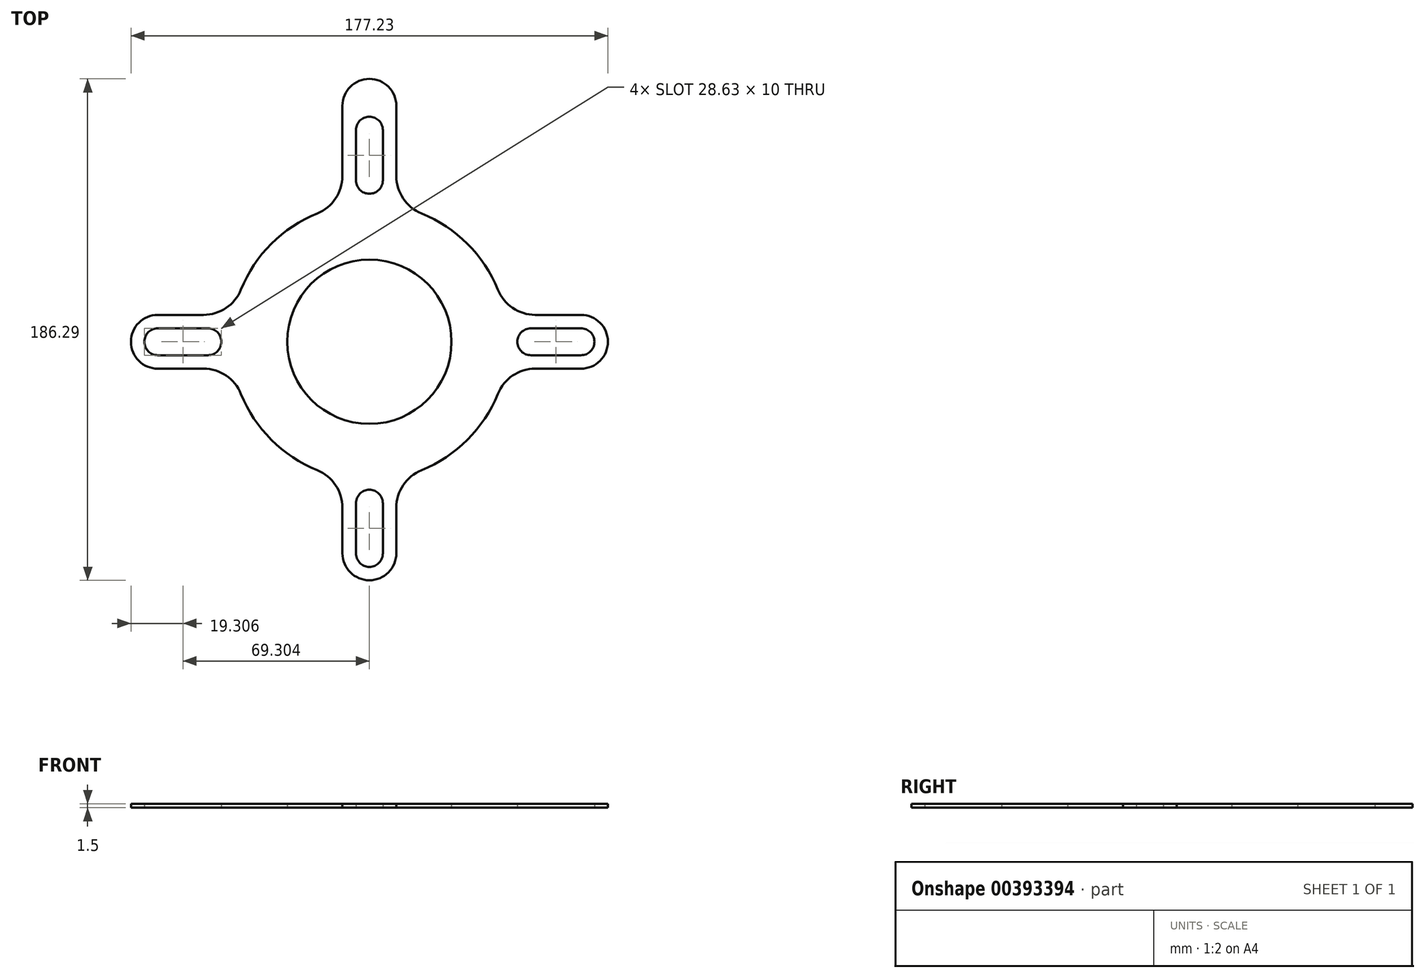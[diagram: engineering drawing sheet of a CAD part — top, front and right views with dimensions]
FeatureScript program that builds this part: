
annotation { "Feature Type Name" : "Feature", "Feature Type Description" : "" }
export const myFeature = defineFeature(function(context is Context, id is Id, definition is map)
    precondition{}
    {
        {
            var Q0;
            Q0=qCreatedBy(makeId("Top.planeOp"),FACE);
            var sketch = newSketch(context, id + "F0", { "sketchPlane" : qUnion([Q0])});
            skCircle(sketch, "E0", {"center": v(0, 0) * mm, "radius": 30.5 * mm});
            skArc(sketch, "E1", {"start": v(-19.36, 47.72) * mm, "mid": v(-36.42, 36.42) * mm, "end": v(-47.72, 19.36) * mm});
            skLineSegment(sketch, "E2", {"start": v(0, 0) * mm, "end": v(0, 75.54) * mm, "construction": true});
            skLineSegment(sketch, "E3", {"start": v(0, 0) * mm, "end": v(88.56, 0) * mm, "construction": true});
            skLineSegment(sketch, "E4", {"start": v(-10, 61.62) * mm, "end": v(-10, 76.12) * mm});
            skLineSegment(sketch, "E5", {"start": v(0, 97.68) * mm, "end": v(0, 97.68) * mm});
            skLineSegment(sketch, "E6", {"start": v(10, 76.12) * mm, "end": v(10, 61.62) * mm});
            skPoint(sketch, "E7.visualSharp", {"position": v(-10, 50.52) * mm});
            skArc(sketch, "E7.filletArc", {"start": v(-19.36, 47.72) * mm, "mid": v(-12.56, 53.24) * mm, "end": v(-10, 61.62) * mm});
            skPoint(sketch, "E8.visualSharp", {"position": v(10, 50.52) * mm});
            skArc(sketch, "E8.filletArc", {"start": v(10, 61.62) * mm, "mid": v(12.56, 53.24) * mm, "end": v(19.36, 47.72) * mm});
            skLineSegment(sketch, "E9.MirrorCS", {"start": v(10, -78.61) * mm, "end": v(10, -61.62) * mm});
            skLineSegment(sketch, "E10.MirrorCS", {"start": v(-10, -61.62) * mm, "end": v(-10, -78.61) * mm});
            skArc(sketch, "E11.MirrorCS", {"start": v(-19.36, -47.72) * mm, "mid": v(-12.56, -53.24) * mm, "end": v(-10, -61.62) * mm});
            skArc(sketch, "E12.MirrorCS", {"start": v(10, -61.62) * mm, "mid": v(12.56, -53.24) * mm, "end": v(19.36, -47.72) * mm});
            skArc(sketch, "E13.trimOffspring", {"start": v(19.36, -47.72) * mm, "mid": v(36.42, -36.42) * mm, "end": v(47.72, -19.36) * mm});
            skLineSegment(sketch, "E14", {"start": v(0, 0) * mm, "end": v(81.73, 81.73) * mm, "construction": true});
            skLineSegment(sketch, "E15.MirrorCS", {"start": v(78.62, 10) * mm, "end": v(61.62, 10) * mm});
            skArc(sketch, "E16.MirrorCS", {"start": v(61.62, 10) * mm, "mid": v(53.24, 12.56) * mm, "end": v(47.72, 19.36) * mm});
            skLineSegment(sketch, "E17.MirrorCS", {"start": v(61.62, -10) * mm, "end": v(78.62, -10) * mm});
            skArc(sketch, "E18.MirrorCS", {"start": v(47.72, -19.36) * mm, "mid": v(53.24, -12.56) * mm, "end": v(61.62, -10) * mm});
            skArc(sketch, "E19.trimOffspring", {"start": v(47.72, 19.36) * mm, "mid": v(36.42, 36.42) * mm, "end": v(19.36, 47.72) * mm});
            skLineSegment(sketch, "E20.MirrorCS", {"start": v(-78.61, 10) * mm, "end": v(-61.62, 10) * mm});
            skLineSegment(sketch, "E21.MirrorCS", {"start": v(-61.62, -10) * mm, "end": v(-78.61, -10) * mm});
            skArc(sketch, "E22.MirrorCS", {"start": v(-61.62, 10) * mm, "mid": v(-53.24, 12.56) * mm, "end": v(-47.72, 19.36) * mm});
            skArc(sketch, "E23.MirrorCS", {"start": v(-47.72, -19.36) * mm, "mid": v(-53.24, -12.56) * mm, "end": v(-61.62, -10) * mm});
            skArc(sketch, "E24.trimOffspring", {"start": v(-47.72, -19.36) * mm, "mid": v(-36.42, -36.42) * mm, "end": v(-19.36, -47.72) * mm});
            skCircle(sketch, "E25", {"center": v(0, 0) * mm, "radius": 65 * mm, "construction": true});
            skLineSegment(sketch, "E26", {"start": v(-10, 61.62) * mm, "end": v(10, 61.62) * mm, "construction": true});
            skEllipse(sketch, "E27", {"center": v(0, 0) * mm, "majorRadius": 30.5 * mm, "minorRadius": 28 * mm, "majorAxis": v(0, 1), "construction": true});
            skLineSegment(sketch, "E28", {"start": v(-10, 65.62) * mm, "end": v(-5, 65.62) * mm});
            skLineSegment(sketch, "E29", {"start": v(-10, 76.12) * mm, "end": v(-5, 76.12) * mm});
            skPoint(sketch, "E30.visualSharp", {"position": v(-10, 97.68) * mm});
            skArc(sketch, "E30.filletArc", {"start": v(0, 97.68) * mm, "mid": v(-7.07, 94.75) * mm, "end": v(-10, 87.68) * mm});
            skPoint(sketch, "E31.visualSharp", {"position": v(10, 97.68) * mm});
            skArc(sketch, "E31.filletArc", {"start": v(10, 87.68) * mm, "mid": v(7.07, 94.75) * mm, "end": v(0, 97.68) * mm});
            skLineSegment(sketch, "E32.MirrorCS", {"start": v(76.12, -10) * mm, "end": v(76.12, -5) * mm});
            skLineSegment(sketch, "E33.MirrorCS", {"start": v(65.62, -10) * mm, "end": v(65.62, -5) * mm});
            skLineSegment(sketch, "E34.MirrorCS", {"start": v(-10, -76.12) * mm, "end": v(-5, -76.12) * mm});
            skLineSegment(sketch, "E35.MirrorCS", {"start": v(-10, -65.62) * mm, "end": v(-5, -65.62) * mm});
            skLineSegment(sketch, "E36.MirrorCS", {"start": v(-65.62, -10) * mm, "end": v(-65.62, -5) * mm});
            skLineSegment(sketch, "E37.MirrorCS", {"start": v(-76.12, -10) * mm, "end": v(-76.12, -5) * mm});
            skPoint(sketch, "E38.centerSnap0", {"position": v(0, 97.68) * mm});
            skLineSegment(sketch, "E39", {"start": v(-10, 76.12) * mm, "end": v(0, 87.68) * mm, "construction": true});
            skLineSegment(sketch, "E40", {"start": v(10, 76.12) * mm, "end": v(0, 87.68) * mm, "construction": true});
            skPoint(sketch, "E41.visualSharp", {"position": v(85.12, 10) * mm});
            skLineSegment(sketch, "E41.filletArc", {"start": v(88.05, 10) * mm, "end": v(88.05, 10) * mm});
            skPoint(sketch, "E42.visualSharp", {"position": v(85.12, -10) * mm});
            skLineSegment(sketch, "E42.filletArc", {"start": v(88.05, -10) * mm, "end": v(88.05, -10) * mm});
            skLineSegment(sketch, "E43.MirrorCS", {"start": v(-88.05, 10) * mm, "end": v(-88.05, 10) * mm});
            skLineSegment(sketch, "E44.MirrorCS", {"start": v(-88.05, -10) * mm, "end": v(-88.05, -10) * mm});
            skLineSegment(sketch, "E45", {"start": v(0, 0) * mm, "end": v(75.2, -75.2) * mm, "construction": true});
            skLineSegment(sketch, "E46.MirrorCS", {"start": v(10, -88.05) * mm, "end": v(10, -88.05) * mm});
            skLineSegment(sketch, "E47.MirrorCS", {"start": v(-10, -88.05) * mm, "end": v(-10, -88.05) * mm});
            skLineSegment(sketch, "E48.trimOffspring", {"start": v(88.62, 0) * mm, "end": v(88.62, 0) * mm});
            skLineSegment(sketch, "E49.trimOffspring", {"start": v(-88.61, 0) * mm, "end": v(-88.61, 0) * mm});
            skLineSegment(sketch, "E50.trimOffspring", {"start": v(0, -88.61) * mm, "end": v(0, -88.61) * mm});
            skArc(sketch, "E51.filletArc", {"start": v(88.62, 0) * mm, "mid": v(85.7, 7.07) * mm, "end": v(78.62, 10) * mm});
            skArc(sketch, "E52.filletArc", {"start": v(78.62, -10) * mm, "mid": v(85.7, -7.07) * mm, "end": v(88.62, 0) * mm});
            skArc(sketch, "E53.filletArc", {"start": v(-10, -78.61) * mm, "mid": v(-7.07, -85.68) * mm, "end": v(0, -88.61) * mm});
            skArc(sketch, "E54.filletArc", {"start": v(0, -88.61) * mm, "mid": v(7.07, -85.68) * mm, "end": v(10, -78.61) * mm});
            skArc(sketch, "E55.filletArc", {"start": v(-88.61, 0) * mm, "mid": v(-85.68, -7.07) * mm, "end": v(-78.61, -10) * mm});
            skArc(sketch, "E56.filletArc", {"start": v(-78.61, 10) * mm, "mid": v(-85.68, 7.07) * mm, "end": v(-88.61, 0) * mm});
            skLineSegment(sketch, "E57.bottom", {"start": v(78.62, 5) * mm, "end": v(59.99, 5) * mm});
            skLineSegment(sketch, "E57.top", {"start": v(78.62, -5) * mm, "end": v(59.99, -5) * mm});
            skLineSegment(sketch, "E57.left", {"start": v(83.62, 0) * mm, "end": v(83.62, 0) * mm});
            skLineSegment(sketch, "E57.right", {"start": v(54.99, 0) * mm, "end": v(54.99, 0) * mm});
            skPoint(sketch, "E57.middle", {"position": v(69.3, 0) * mm});
            skPoint(sketch, "E58.visualSharp", {"position": v(83.62, 5) * mm});
            skArc(sketch, "E58.filletArc", {"start": v(83.62, 0) * mm, "mid": v(82.16, 3.54) * mm, "end": v(78.62, 5) * mm});
            skPoint(sketch, "E59.visualSharp", {"position": v(83.62, -5) * mm});
            skArc(sketch, "E59.filletArc", {"start": v(78.62, -5) * mm, "mid": v(82.16, -3.54) * mm, "end": v(83.62, 0) * mm});
            skPoint(sketch, "E60.visualSharp", {"position": v(54.99, 5) * mm});
            skArc(sketch, "E60.filletArc", {"start": v(59.99, 5) * mm, "mid": v(56.45, 3.54) * mm, "end": v(54.99, 0) * mm});
            skPoint(sketch, "E61.visualSharp", {"position": v(54.99, -5) * mm});
            skArc(sketch, "E61.filletArc", {"start": v(54.99, 0) * mm, "mid": v(56.45, -3.54) * mm, "end": v(59.99, -5) * mm});
            skLineSegment(sketch, "E62.MirrorCS", {"start": v(0, -83.62) * mm, "end": v(0, -83.62) * mm});
            skLineSegment(sketch, "E63.MirrorCS", {"start": v(-5, -78.62) * mm, "end": v(-5, -59.99) * mm});
            skLineSegment(sketch, "E64.MirrorCS", {"start": v(0, -54.99) * mm, "end": v(0, -54.99) * mm});
            skLineSegment(sketch, "E65.MirrorCS", {"start": v(5, -78.62) * mm, "end": v(5, -59.99) * mm});
            skArc(sketch, "E66.MirrorCS", {"start": v(0, -54.99) * mm, "mid": v(3.54, -56.45) * mm, "end": v(5, -59.99) * mm});
            skArc(sketch, "E67.MirrorCS", {"start": v(-5, -59.99) * mm, "mid": v(-3.54, -56.45) * mm, "end": v(0, -54.99) * mm});
            skArc(sketch, "E68.MirrorCS", {"start": v(0, -83.62) * mm, "mid": v(-3.54, -82.16) * mm, "end": v(-5, -78.62) * mm});
            skArc(sketch, "E69.MirrorCS", {"start": v(5, -78.62) * mm, "mid": v(3.54, -82.16) * mm, "end": v(0, -83.62) * mm});
            skLineSegment(sketch, "E70.MirrorCS", {"start": v(-83.62, 0) * mm, "end": v(-83.62, 0) * mm});
            skArc(sketch, "E71.MirrorCS", {"start": v(-83.62, 0) * mm, "mid": v(-82.16, 3.54) * mm, "end": v(-78.62, 5) * mm});
            skArc(sketch, "E72.MirrorCS", {"start": v(-78.62, -5) * mm, "mid": v(-82.16, -3.54) * mm, "end": v(-83.62, 0) * mm});
            skLineSegment(sketch, "E73.MirrorCS", {"start": v(-78.62, -5) * mm, "end": v(-59.99, -5) * mm});
            skLineSegment(sketch, "E74.MirrorCS", {"start": v(-78.62, 5) * mm, "end": v(-59.99, 5) * mm});
            skArc(sketch, "E75.MirrorCS", {"start": v(-59.99, 5) * mm, "mid": v(-56.45, 3.54) * mm, "end": v(-54.99, 0) * mm});
            skLineSegment(sketch, "E76.MirrorCS", {"start": v(-54.99, 0) * mm, "end": v(-54.99, 0) * mm});
            skArc(sketch, "E77.MirrorCS", {"start": v(-54.99, 0) * mm, "mid": v(-56.45, -3.54) * mm, "end": v(-59.99, -5) * mm});
            skLineSegment(sketch, "E78.MirrorCS", {"start": v(0, 54.99) * mm, "end": v(0, 54.99) * mm});
            skArc(sketch, "E79.MirrorCS", {"start": v(0, 54.99) * mm, "mid": v(3.54, 56.45) * mm, "end": v(5, 59.99) * mm});
            skArc(sketch, "E80.MirrorCS", {"start": v(-5, 59.99) * mm, "mid": v(-3.54, 56.45) * mm, "end": v(0, 54.99) * mm});
            skLineSegment(sketch, "E81.trimOffspring", {"start": v(-5, 76.12) * mm, "end": v(-5, 59.99) * mm});
            skLineSegment(sketch, "E82.trimOffspring", {"start": v(5, 76.12) * mm, "end": v(5, 59.99) * mm});
            skLineSegment(sketch, "E83.trimOffspring", {"start": v(5, 65.62) * mm, "end": v(10, 65.62) * mm});
            skLineSegment(sketch, "E84.trimOffspring", {"start": v(5, 76.12) * mm, "end": v(10, 76.12) * mm});
            skLineSegment(sketch, "E85.trimOffspring", {"start": v(65.62, 5) * mm, "end": v(65.62, 10) * mm});
            skLineSegment(sketch, "E86.trimOffspring", {"start": v(76.12, 5) * mm, "end": v(76.12, 10) * mm});
            skLineSegment(sketch, "E87.trimOffspring", {"start": v(-65.62, 5) * mm, "end": v(-65.62, 10) * mm});
            skLineSegment(sketch, "E88.trimOffspring", {"start": v(-76.12, 5) * mm, "end": v(-76.12, 10) * mm});
            skLineSegment(sketch, "E89.trimOffspring", {"start": v(5, -76.12) * mm, "end": v(10, -76.12) * mm});
            skLineSegment(sketch, "E90.trimOffspring", {"start": v(5, -65.62) * mm, "end": v(10, -65.62) * mm});
            skLineSegment(sketch, "E91", {"start": v(-10, 76.12) * mm, "end": v(-10, 87.68) * mm});
            skLineSegment(sketch, "E92", {"start": v(10, 87.68) * mm, "end": v(10, 76.12) * mm});
            skArc(sketch, "E93.MirrorCS", {"start": v(0, 83.62) * mm, "mid": v(3.54, 82.16) * mm, "end": v(5, 78.62) * mm});
            skArc(sketch, "E94.MirrorCS", {"start": v(-5, 78.62) * mm, "mid": v(-3.54, 82.16) * mm, "end": v(0, 83.62) * mm});
            skLineSegment(sketch, "E95.MirrorCS", {"start": v(0, 83.62) * mm, "end": v(0, 83.62) * mm});
            skLineSegment(sketch, "E96", {"start": v(-5, 78.62) * mm, "end": v(-5, 76.12) * mm});
            skLineSegment(sketch, "E97", {"start": v(5, 78.62) * mm, "end": v(5, 76.12) * mm});
            skCircle(sketch, "E98", {"center": v(0, 0) * mm, "radius": 68.5 * mm, "construction": true});
            skSolve(sketch);
        }
        {
            var Q0;
            Q0=makeQuery(id+"F0.imprint","IMPRINT",FACE,{"disambiguationData":[TD([[makeQuery(id+"F0.imprint","IMPRINT",EDGE,{"derivedFrom":sQuery(id+"F0.wireOp",EDGE,"E0")}),-1.0]])]});
            var Q1;
            Q1=makeQuery(id+"F0.imprint","IMPRINT",FACE,{"disambiguationData":[TD([[makeQuery(id+"F0.imprint","IMPRINT",EDGE,{"derivedFrom":sQuery(id+"F0.wireOp",EDGE,"E5")}),-1.0]])]});
            var Q2;
            {var subQ2=sQuery(id+"F0.wireOp",EDGE,"E83.trimOffspring");Q2=makeQuery(id+"F0.imprint","IMPRINT",FACE,{"disambiguationData":[TD([[makeQuery(id+"F0.imprint","IMPRINT",EDGE,{"derivedFrom":subQ2}),1.0]])]});}
            var Q3;
            {var subQ2=sQuery(id+"F0.wireOp",EDGE,"E28");Q3=makeQuery(id+"F0.imprint","IMPRINT",FACE,{"disambiguationData":[TD([[makeQuery(id+"F0.imprint","IMPRINT",EDGE,{"derivedFrom":subQ2}),1.0]])]});}
            var Q4;
            {var subQ0=sQuery(id+"F0.wireOp",EDGE,"E85.trimOffspring");Q4=makeQuery(id+"F0.imprint","IMPRINT",FACE,{"disambiguationData":[TD([[makeQuery(id+"F0.imprint","IMPRINT",EDGE,{"derivedFrom":subQ0}),-1.0]])]});}
            var Q5;
            {var subQ0=sQuery(id+"F0.wireOp",EDGE,"E32.MirrorCS");Q5=makeQuery(id+"F0.imprint","IMPRINT",FACE,{"disambiguationData":[TD([[makeQuery(id+"F0.imprint","IMPRINT",EDGE,{"derivedFrom":subQ0}),1.0]])]});}
            var Q6;
            {var subQ1=sQuery(id+"F0.wireOp",EDGE,"E32.MirrorCS");Q6=makeQuery(id+"F0.imprint","IMPRINT",FACE,{"disambiguationData":[TD([[makeQuery(id+"F0.imprint","IMPRINT",EDGE,{"derivedFrom":subQ1}),-1.0]])]});}
            var Q7;
            {var subQ0=sQuery(id+"F0.wireOp",EDGE,"E36.MirrorCS");Q7=makeQuery(id+"F0.imprint","IMPRINT",FACE,{"disambiguationData":[TD([[makeQuery(id+"F0.imprint","IMPRINT",EDGE,{"derivedFrom":subQ0}),1.0]])]});}
            var Q8;
            {var subQ0=sQuery(id+"F0.wireOp",EDGE,"E87.trimOffspring");Q8=makeQuery(id+"F0.imprint","IMPRINT",FACE,{"disambiguationData":[TD([[makeQuery(id+"F0.imprint","IMPRINT",EDGE,{"derivedFrom":subQ0}),1.0]])]});}
            var Q9;
            {var subQ3=sQuery(id+"F0.wireOp",EDGE,"E37.MirrorCS");Q9=makeQuery(id+"F0.imprint","IMPRINT",FACE,{"disambiguationData":[TD([[makeQuery(id+"F0.imprint","IMPRINT",EDGE,{"derivedFrom":subQ3}),1.0]])]});}
            var Q10;
            {var subQ0=sQuery(id+"F0.wireOp",EDGE,"E34.MirrorCS");Q10=makeQuery(id+"F0.imprint","IMPRINT",FACE,{"disambiguationData":[TD([[makeQuery(id+"F0.imprint","IMPRINT",EDGE,{"derivedFrom":subQ0}),1.0]])]});}
            var Q11;
            {var subQ0=sQuery(id+"F0.wireOp",EDGE,"E89.trimOffspring");Q11=makeQuery(id+"F0.imprint","IMPRINT",FACE,{"disambiguationData":[TD([[makeQuery(id+"F0.imprint","IMPRINT",EDGE,{"derivedFrom":subQ0}),1.0]])]});}
            var Q12;
            {var subQ5=sQuery(id+"F0.wireOp",EDGE,"E34.MirrorCS");Q12=makeQuery(id+"F0.imprint","IMPRINT",FACE,{"disambiguationData":[TD([[makeQuery(id+"F0.imprint","IMPRINT",EDGE,{"derivedFrom":subQ5}),-1.0]])]});}
            var Q13;
            Q13=makeQuery(id+"F0.imprint","IMPRINT",FACE,{"disambiguationData":[TD([[makeQuery(id+"F0.imprint","IMPRINT",EDGE,{"derivedFrom":sQuery(id+"F0.wireOp",EDGE,"E29")}),1.0]])]});
            extrude(context, id + "F1", {"entities" : qUnion([Q0, Q1, Q2, Q3, Q4, Q5, Q6, Q7, Q8, Q9, Q10, Q11, Q12, Q13]), "depth" : 1.5 * mm});
        }
    });
